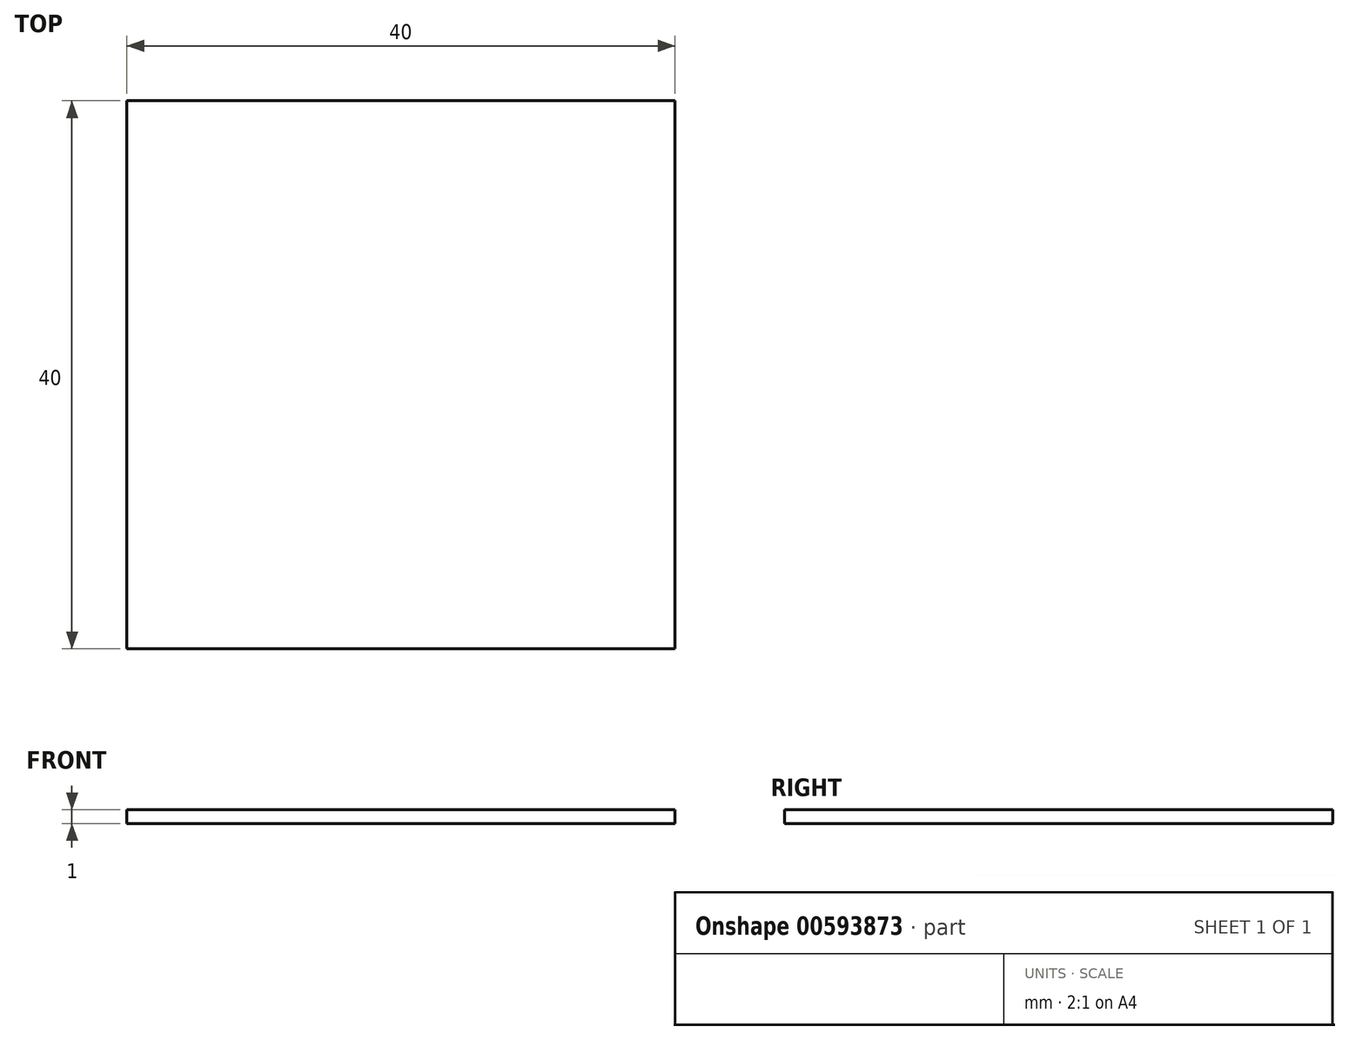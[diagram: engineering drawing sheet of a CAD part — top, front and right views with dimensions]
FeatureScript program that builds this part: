
annotation { "Feature Type Name" : "Feature", "Feature Type Description" : "" }
export const myFeature = defineFeature(function(context is Context, id is Id, definition is map)
    precondition{}
    {
        {
            var Q0;
            Q0=qCreatedBy(makeId("Top.planeOp"),FACE);
            var sketch = newSketch(context, id + "F0", { "sketchPlane" : qUnion([Q0])});
            skLineSegment(sketch, "E0.bottom", {"start": v(20, -20) * mm, "end": v(-20, -20) * mm});
            skLineSegment(sketch, "E0.top", {"start": v(20, 20) * mm, "end": v(-20, 20) * mm});
            skLineSegment(sketch, "E0.left", {"start": v(20, -20) * mm, "end": v(20, 20) * mm});
            skLineSegment(sketch, "E0.right", {"start": v(-20, -20) * mm, "end": v(-20, 20) * mm});
            skPoint(sketch, "E0.middle", {"position": v(0, 0) * mm});
            skSolve(sketch);
        }
        {
            var Q0;
            Q0 = qSketchRegion(id + "F0", true);
            extrude(context, id + "F1", {"entities" : qUnion([Q0]), "depth" : 1 * mm, "offsetDistance" : 25 * mm});
        }
    });
